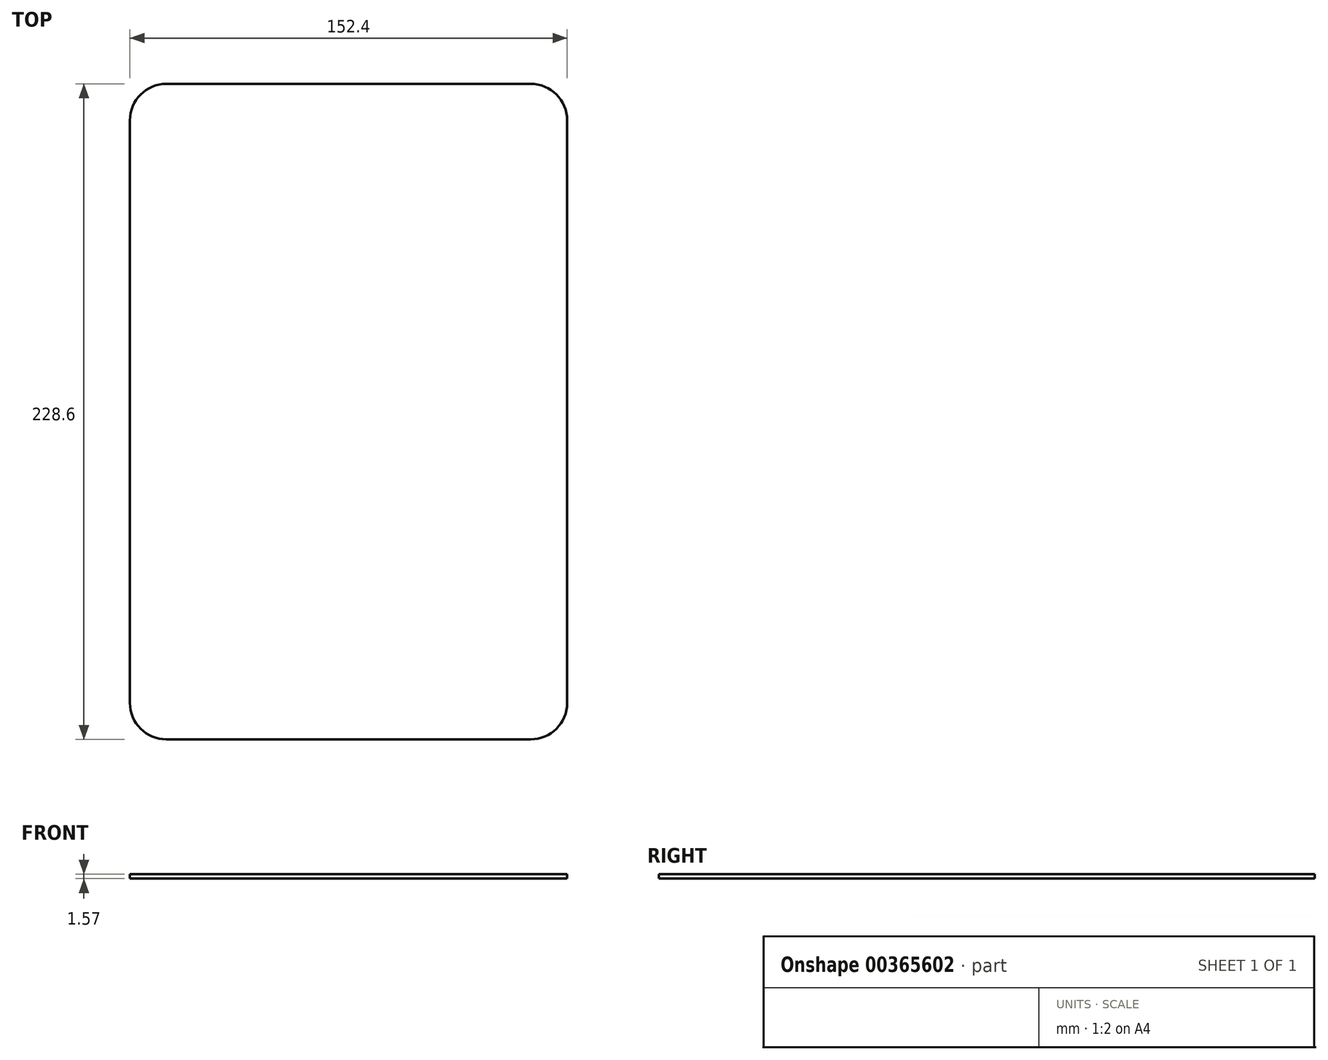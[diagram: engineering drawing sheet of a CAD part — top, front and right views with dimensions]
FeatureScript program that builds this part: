
annotation { "Feature Type Name" : "Feature", "Feature Type Description" : "" }
export const myFeature = defineFeature(function(context is Context, id is Id, definition is map)
    precondition{}
    {
        {
            var Q0;
            Q0=qCreatedBy(makeId("Top.planeOp"),FACE);
            var sketch = newSketch(context, id + "F0", { "sketchPlane" : qUnion([Q0])});
            skLineSegment(sketch, "E0.bottom", {"start": v(-76.2, 0) * mm, "end": v(76.2, 0) * mm});
            skLineSegment(sketch, "E0.top", {"start": v(-76.2, -228.6) * mm, "end": v(76.2, -228.6) * mm});
            skLineSegment(sketch, "E0.left", {"start": v(-76.2, 0) * mm, "end": v(-76.2, -228.6) * mm});
            skLineSegment(sketch, "E0.right", {"start": v(76.2, 0) * mm, "end": v(76.2, -228.6) * mm});
            skSolve(sketch);
        }
        {
            var Q0;
            Q0=makeQuery(id+"F0.imprint","IMPRINT",FACE,{"disambiguationData":[TD([[makeQuery(id+"F0.imprint","IMPRINT",EDGE,{"derivedFrom":sQuery(id+"F0.wireOp",EDGE,"E0.bottom")}),-1.0]])]});
            extrude(context, id + "F1", {"entities" : qUnion([Q0]), "depth" : 1.57 * mm, "offsetDistance" : 25.4 * mm});
        }
        {
            var Q0;
            Q0=makeQuery(id+"F1.opExtrude","SWEPT_EDGE",EDGE,{"disambiguationData":[OSD([sQuery(id+"F0.wireOp",EDGE,"E0.top"),sQuery(id+"F0.wireOp",EDGE,"E0.right")])]});
            var Q1;
            Q1=makeQuery(id+"F1.opExtrude","SWEPT_EDGE",EDGE,{"disambiguationData":[OSD([sQuery(id+"F0.wireOp",EDGE,"E0.bottom"),sQuery(id+"F0.wireOp",EDGE,"E0.right")])]});
            var Q2;
            Q2=makeQuery(id+"F1.opExtrude","SWEPT_EDGE",EDGE,{"disambiguationData":[OSD([sQuery(id+"F0.wireOp",EDGE,"E0.bottom"),sQuery(id+"F0.wireOp",EDGE,"E0.left")])]});
            var Q3;
            Q3=makeQuery(id+"F1.opExtrude","SWEPT_EDGE",EDGE,{"disambiguationData":[OSD([sQuery(id+"F0.wireOp",EDGE,"E0.top"),sQuery(id+"F0.wireOp",EDGE,"E0.left")])]});
            fillet(context, id + "F2", {"entities" : qUnion([Q0, Q1, Q2, Q3]), "radius" : 12.7 * mm, "tangentPropagation" : true, "allowEdgeOverflow" : false});
        }
    });
